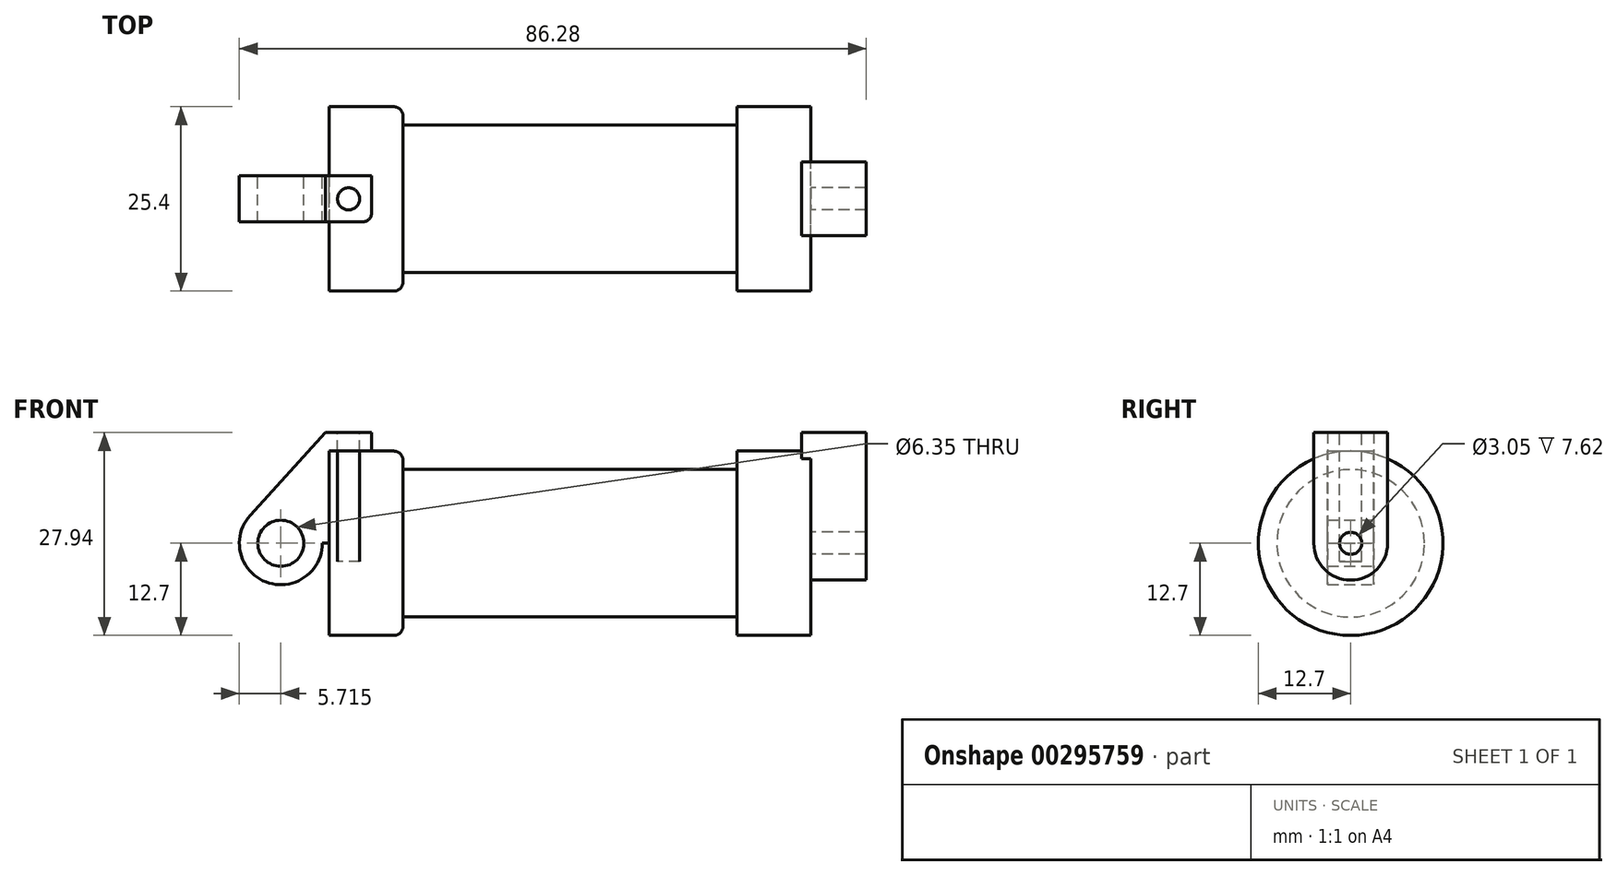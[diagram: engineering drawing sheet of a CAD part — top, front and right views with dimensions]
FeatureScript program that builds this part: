
annotation { "Feature Type Name" : "Feature", "Feature Type Description" : "" }
export const myFeature = defineFeature(function(context is Context, id is Id, definition is map)
    precondition{}
    {
        {
            var Q0;
            Q0=qCreatedBy(makeId("Front.planeOp"),FACE);
            var sketch = newSketch(context, id + "F0", { "sketchPlane" : qUnion([Q0])});
            skLineSegment(sketch, "E0", {"start": v(0, 0) * mm, "end": v(0, 12.7) * mm});
            skLineSegment(sketch, "E1", {"start": v(0, 12.7) * mm, "end": v(10.16, 12.7) * mm});
            skLineSegment(sketch, "E2", {"start": v(10.16, 12.7) * mm, "end": v(10.16, 10.16) * mm});
            skLineSegment(sketch, "E3", {"start": v(10.16, 10.16) * mm, "end": v(56.13, 10.16) * mm});
            skLineSegment(sketch, "E4", {"start": v(56.13, 10.16) * mm, "end": v(56.13, 12.7) * mm});
            skLineSegment(sketch, "E5", {"start": v(56.13, 12.7) * mm, "end": v(66.3, 12.7) * mm});
            skLineSegment(sketch, "E6", {"start": v(66.3, 12.7) * mm, "end": v(66.3, 0) * mm});
            skLineSegment(sketch, "E7", {"start": v(66.3, 0) * mm, "end": v(0, 0) * mm});
            skLineSegment(sketch, "E8", {"start": v(5.84, 15.24) * mm, "end": v(-0.5, 15.24) * mm});
            skLineSegment(sketch, "E9", {"start": v(-0.5, 15.24) * mm, "end": v(-10.88, 3.85) * mm});
            skLineSegment(sketch, "E10", {"start": v(0, 0) * mm, "end": v(-6.65, 0) * mm});
            skCircle(sketch, "E11", {"center": v(-6.65, 0) * mm, "radius": 5.72 * mm});
            skCircle(sketch, "E12", {"center": v(-6.65, 0) * mm, "radius": 3.18 * mm});
            skLineSegment(sketch, "E13", {"start": v(5.84, 15.24) * mm, "end": v(5.84, -9.4) * mm});
            skLineSegment(sketch, "E14", {"start": v(5.84, -9.4) * mm, "end": v(-8.18, -5.5) * mm});
            skSolve(sketch);
        }
        {
            var Q0;
            {var subQ0=sQuery(id+"F0.wireOp",EDGE,"E0");Q0=makeQuery(id+"F0.imprint","IMPRINT",FACE,{"disambiguationData":[TD([[makeQuery(id+"F0.imprint","IMPRINT",EDGE,{"derivedFrom":subQ0}),-1.0]])]});}
            var Q1;
            {var subQ0=sQuery(id+"F0.wireOp",EDGE,"E2");Q1=makeQuery(id+"F0.imprint","IMPRINT",FACE,{"disambiguationData":[TD([[makeQuery(id+"F0.imprint","IMPRINT",EDGE,{"derivedFrom":subQ0}),-1.0]])]});}
            var Q2;
            Q2=sQuery(id+"F0.wireOp",EDGE,"E7");
            revolve(context, id + "F1", {"entities" : qUnion([Q0, Q1]), "axis" : qUnion([Q2]), "revolveType" : RevolveType.FULL});
        }
        {
            var Q0;
            {var subQ1=sQuery(id+"F0.wireOp",EDGE,"E0");Q0=makeQuery(id+"F0.imprint","IMPRINT",FACE,{"disambiguationData":[TD([[makeQuery(id+"F0.imprint","IMPRINT",EDGE,{"derivedFrom":subQ1}),1.0]])]});}
            var Q1;
            {var subQ5=sQuery(id+"F0.wireOp",EDGE,"E12");Q1=makeQuery(id+"F0.imprint","IMPRINT",FACE,{"disambiguationData":[TD([[makeQuery(id+"F0.imprint","IMPRINT",EDGE,{"derivedFrom":subQ5}),-1.0]])]});}
            extrude(context, id + "F2", {"entities" : qUnion([Q0, Q1]), "endBound" : BoundingType.SYMMETRIC, "depth" : 6.35 * mm});
        }
        {
            var Q0;
            Q0=makeQuery(id+"F1.opRevolve","SWEPT_FACE",FACE,{"disambiguationData":[OSD([sQuery(id+"F0.wireOp",EDGE,"E6")])]});
            var sketch = newSketch(context, id + "F3", { "sketchPlane" : qUnion([Q0])});
            skCircle(sketch, "E15", {"center": v(0, 0) * mm, "radius": 1.52 * mm});
            skCircle(sketch, "E16", {"center": v(0, 0) * mm, "radius": 5.08 * mm});
            skLineSegment(sketch, "E17", {"start": v(-5.08, 0) * mm, "end": v(-5.08, 15.24) * mm});
            skLineSegment(sketch, "E18", {"start": v(5.08, 0) * mm, "end": v(5.08, 15.24) * mm});
            skLineSegment(sketch, "E19", {"start": v(-5.08, 15.24) * mm, "end": v(5.08, 15.24) * mm});
            skSolve(sketch);
        }
        {
            var Q0;
            {var subQ0=sQuery(id+"F3.wireOp",EDGE,"E19");Q0=makeQuery(id+"F3.imprint","IMPRINT",FACE,{"disambiguationData":[TD([[makeQuery(id+"F3.imprint","IMPRINT",EDGE,{"derivedFrom":subQ0}),-1.0]])]});}
            extrude(context, id + "F4", {"entities" : qUnion([Q0]), "operationType" : NewBodyOperationType.ADD, "oppositeDirection" : true, "depth" : 1.27 * mm});
        }
        {
            var Q0;
            Q0 = qSketchRegion(id + "F3", true);
            extrude(context, id + "F5", {"entities" : qUnion([Q0]), "operationType" : NewBodyOperationType.ADD, "depth" : 7.62 * mm});
        }
        {
            var Q0;
            Q0=makeQuery(id+"F2.opExtrude","SWEPT_FACE",FACE,{"disambiguationData":[OSD([sQuery(id+"F0.wireOp",EDGE,"E8")])]});
            var sketch = newSketch(context, id + "F6", { "sketchPlane" : qUnion([Q0])});
            skPoint(sketch, "E20.centerSnap0", {"position": v(5.84, 0) * mm});
            skLineSegment(sketch, "E21", {"start": v(2.67, 3.18) * mm, "end": v(2.67, -3.18) * mm, "construction": true});
            skCircle(sketch, "E22", {"center": v(2.67, 0) * mm, "radius": 1.52 * mm});
            skSolve(sketch);
        }
        {
            var Q0;
            {var subQ0=sQuery(id+"F3.wireOp",EDGE,"E19");Q0=makeQuery(id+"F5.boolean.opBoolean","MERGE",FACE,{"derivedFrom":[makeQuery(id+"F4.opExtrude","SWEPT_FACE",FACE,{"disambiguationData":[OSD([subQ0])]}),makeQuery(id+"F5.opExtrude","SWEPT_FACE",FACE,{"disambiguationData":[OSD([subQ0])]})]});}
            var sketch = newSketch(context, id + "F7", { "sketchPlane" : qUnion([Q0])});
            skLineSegment(sketch, "E23", {"start": v(69.47, 5.08) * mm, "end": v(69.47, -5.08) * mm, "construction": true});
            skLineSegment(sketch, "E24", {"start": v(73.91, 0) * mm, "end": v(65.02, 0) * mm, "construction": true});
            skCircle(sketch, "E25", {"center": v(69.47, 0) * mm, "radius": 1.52 * mm});
            skSolve(sketch);
        }
        {
            var Q0;
            Q0=makeQuery(id+"F6.imprint","IMPRINT",FACE,{"disambiguationData":[TD([[makeQuery(id+"F6.imprint","IMPRINT",EDGE,{"derivedFrom":sQuery(id+"F6.wireOp",EDGE,"E22")}),1.0]])]});
            extrude(context, id + "F8", {"entities" : qUnion([Q0]), "oppositeDirection" : true, "depth" : 17.78 * mm});
        }
        {
            var Q0;
            Q0=sQuery(id+"F7.wireOp",EDGE,"E25");
            extrude(context, id + "F9", {"bodyType" : ToolBodyType.SURFACE, "surfaceEntities" : qUnion([Q0]), "oppositeDirection" : true, "depth" : 10.4 * mm});
        }
        {
            var Q0;
            Q0=makeQuery(id+"F1.opRevolve","SWEPT_EDGE",EDGE,{"disambiguationData":[OSD([sQuery(id+"F0.wireOp",EDGE,"E1"),sQuery(id+"F0.wireOp",EDGE,"E2")])]});
            fillet(context, id + "F10", {"entities" : qUnion([Q0]), "radius" : 1.27 * mm, "tangentPropagation" : true, "allowEdgeOverflow" : false});
        }
        {
            var Q0;
            Q0=makeQuery(id+"F2.opExtrude","CAP_EDGE",EDGE,{"disambiguationData":[OSD([sQuery(id+"F0.wireOp",EDGE,"E13")])],"isStart":false});
            fillet(context, id + "F11", {"entities" : qUnion([Q0]), "radius" : 1.27 * mm, "tangentPropagation" : true, "allowEdgeOverflow" : false});
        }
    });
